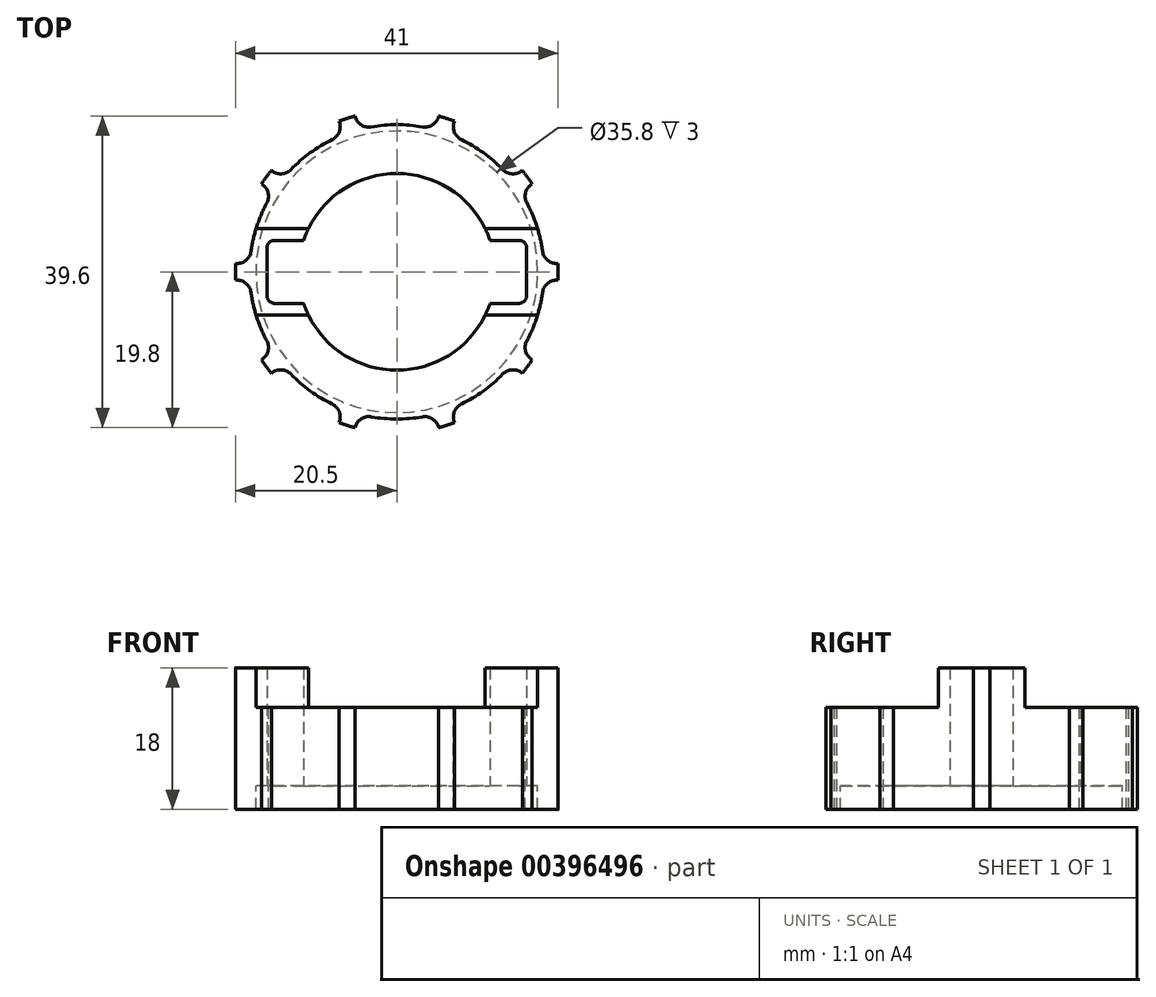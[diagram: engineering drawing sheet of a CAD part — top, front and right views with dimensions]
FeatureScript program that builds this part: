
annotation { "Feature Type Name" : "Feature", "Feature Type Description" : "" }
export const myFeature = defineFeature(function(context is Context, id is Id, definition is map)
    precondition{}
    {
        {
            var Q0;
            Q0=qCreatedBy(makeId("Top.planeOp"),FACE);
            var sketch = newSketch(context, id + "F0", { "sketchPlane" : qUnion([Q0])});
            skCircle(sketch, "E0", {"center": v(0, 0) * mm, "radius": 17.9 * mm});
            skCircle(sketch, "E1", {"center": v(0, 0) * mm, "radius": 20.5 * mm});
            skCircle(sketch, "E2", {"center": v(0, 0) * mm, "radius": 12.5 * mm});
            skLineSegment(sketch, "E3", {"start": v(0, 0) * mm, "end": v(0, 4) * mm, "construction": true});
            skLineSegment(sketch, "E4", {"start": v(0, 0) * mm, "end": v(16.5, 0) * mm, "construction": true});
            skLineSegment(sketch, "E5", {"start": v(0, 0) * mm, "end": v(-16.5, 0) * mm, "construction": true});
            skLineSegment(sketch, "E6", {"start": v(16.5, 0) * mm, "end": v(16.5, 3) * mm});
            skLineSegment(sketch, "E7", {"start": v(-16.5, 0) * mm, "end": v(-16.5, 3) * mm});
            skLineSegment(sketch, "E8", {"start": v(-15.5, 4) * mm, "end": v(-11.84, 4) * mm});
            skLineSegment(sketch, "E9", {"start": v(0, 0) * mm, "end": v(0, 20.5) * mm, "construction": true});
            skLineSegment(sketch, "E10", {"start": v(0, 0) * mm, "end": v(-3.56, 20.19) * mm, "construction": true});
            skArc(sketch, "E11", {"start": v(-5.32, 19.8) * mm, "mid": v(-4.56, 18.7) * mm, "end": v(-3.25, 18.42) * mm});
            skArc(sketch, "E12", {"start": v(-3.25, 18.42) * mm, "mid": v(-1.63, 18.63) * mm, "end": v(0, 18.7) * mm});
            skArc(sketch, "E13.MirrorCS", {"start": v(5.32, 19.8) * mm, "mid": v(4.56, 18.7) * mm, "end": v(3.25, 18.42) * mm});
            skArc(sketch, "E14.MirrorCS", {"start": v(3.25, 18.42) * mm, "mid": v(1.63, 18.63) * mm, "end": v(0, 18.7) * mm});
            skArc(sketch, "E15.1.0", {"start": v(-13.45, 13) * mm, "mid": v(-12.27, 14.11) * mm, "end": v(-11, 15.13) * mm});
            skArc(sketch, "E15.1.1", {"start": v(-15.94, 12.9) * mm, "mid": v(-14.68, 12.44) * mm, "end": v(-13.45, 13) * mm});
            skArc(sketch, "E15.1.2", {"start": v(-8.2, 16.8) * mm, "mid": v(-9.63, 16.03) * mm, "end": v(-11, 15.13) * mm});
            skArc(sketch, "E15.1.3", {"start": v(-7.34, 19.14) * mm, "mid": v(-7.3, 17.8) * mm, "end": v(-8.2, 16.8) * mm});
            skArc(sketch, "E15.2.0", {"start": v(-18.52, 2.6) * mm, "mid": v(-18.22, 4.2) * mm, "end": v(-17.78, 5.78) * mm});
            skArc(sketch, "E15.2.1", {"start": v(-20.47, 1.06) * mm, "mid": v(-19.19, 1.44) * mm, "end": v(-18.52, 2.6) * mm});
            skArc(sketch, "E15.2.2", {"start": v(-16.51, 8.78) * mm, "mid": v(-17.21, 7.3) * mm, "end": v(-17.78, 5.78) * mm});
            skArc(sketch, "E15.2.3", {"start": v(-17.19, 11.17) * mm, "mid": v(-16.37, 10.11) * mm, "end": v(-16.51, 8.78) * mm});
            skArc(sketch, "E16.2.3.0", {"start": v(-16.51, -8.78) * mm, "mid": v(-17.21, -7.3) * mm, "end": v(-17.78, -5.78) * mm});
            skArc(sketch, "E16.4.3.0", {"start": v(-17.19, -11.17) * mm, "mid": v(-16.37, -10.11) * mm, "end": v(-16.51, -8.78) * mm});
            skArc(sketch, "E16.8.3.0", {"start": v(-18.52, -2.6) * mm, "mid": v(-18.22, -4.2) * mm, "end": v(-17.78, -5.78) * mm});
            skArc(sketch, "E16.12.3.0", {"start": v(-20.47, -1.06) * mm, "mid": v(-19.19, -1.44) * mm, "end": v(-18.52, -2.6) * mm});
            skArc(sketch, "E16.2.4.0", {"start": v(-8.2, -16.8) * mm, "mid": v(-9.63, -16.03) * mm, "end": v(-11, -15.13) * mm});
            skArc(sketch, "E16.4.4.0", {"start": v(-7.34, -19.14) * mm, "mid": v(-7.3, -17.8) * mm, "end": v(-8.2, -16.8) * mm});
            skArc(sketch, "E16.8.4.0", {"start": v(-13.45, -13) * mm, "mid": v(-12.27, -14.11) * mm, "end": v(-11, -15.13) * mm});
            skArc(sketch, "E16.12.4.0", {"start": v(-15.94, -12.9) * mm, "mid": v(-14.68, -12.44) * mm, "end": v(-13.45, -13) * mm});
            skArc(sketch, "E16.2.5.0", {"start": v(3.25, -18.42) * mm, "mid": v(1.63, -18.63) * mm, "end": v(0, -18.7) * mm});
            skArc(sketch, "E16.4.5.0", {"start": v(5.32, -19.8) * mm, "mid": v(4.56, -18.7) * mm, "end": v(3.25, -18.42) * mm});
            skArc(sketch, "E16.8.5.0", {"start": v(-3.25, -18.42) * mm, "mid": v(-1.63, -18.63) * mm, "end": v(0, -18.7) * mm});
            skArc(sketch, "E16.12.5.0", {"start": v(-5.32, -19.8) * mm, "mid": v(-4.56, -18.7) * mm, "end": v(-3.25, -18.42) * mm});
            skArc(sketch, "E16.2.6.0", {"start": v(13.45, -13) * mm, "mid": v(12.27, -14.11) * mm, "end": v(11, -15.13) * mm});
            skArc(sketch, "E16.4.6.0", {"start": v(15.94, -12.9) * mm, "mid": v(14.68, -12.44) * mm, "end": v(13.45, -13) * mm});
            skArc(sketch, "E16.8.6.0", {"start": v(8.2, -16.8) * mm, "mid": v(9.63, -16.03) * mm, "end": v(11, -15.13) * mm});
            skArc(sketch, "E16.12.6.0", {"start": v(7.34, -19.14) * mm, "mid": v(7.3, -17.8) * mm, "end": v(8.2, -16.8) * mm});
            skArc(sketch, "E16.2.7.0", {"start": v(18.52, -2.6) * mm, "mid": v(18.22, -4.2) * mm, "end": v(17.78, -5.78) * mm});
            skArc(sketch, "E16.4.7.0", {"start": v(20.47, -1.06) * mm, "mid": v(19.19, -1.44) * mm, "end": v(18.52, -2.6) * mm});
            skArc(sketch, "E16.8.7.0", {"start": v(16.51, -8.78) * mm, "mid": v(17.21, -7.3) * mm, "end": v(17.78, -5.78) * mm});
            skArc(sketch, "E16.12.7.0", {"start": v(17.19, -11.17) * mm, "mid": v(16.37, -10.11) * mm, "end": v(16.51, -8.78) * mm});
            skArc(sketch, "E16.2.8.0", {"start": v(16.51, 8.78) * mm, "mid": v(17.21, 7.3) * mm, "end": v(17.78, 5.78) * mm});
            skArc(sketch, "E16.4.8.0", {"start": v(17.19, 11.17) * mm, "mid": v(16.37, 10.11) * mm, "end": v(16.51, 8.78) * mm});
            skArc(sketch, "E16.8.8.0", {"start": v(18.52, 2.6) * mm, "mid": v(18.22, 4.2) * mm, "end": v(17.78, 5.78) * mm});
            skArc(sketch, "E16.12.8.0", {"start": v(20.47, 1.06) * mm, "mid": v(19.19, 1.44) * mm, "end": v(18.52, 2.6) * mm});
            skArc(sketch, "E16.2.9.0", {"start": v(8.2, 16.8) * mm, "mid": v(9.63, 16.03) * mm, "end": v(11, 15.13) * mm});
            skArc(sketch, "E16.4.9.0", {"start": v(7.34, 19.14) * mm, "mid": v(7.3, 17.8) * mm, "end": v(8.2, 16.8) * mm});
            skArc(sketch, "E16.8.9.0", {"start": v(13.45, 13) * mm, "mid": v(12.27, 14.11) * mm, "end": v(11, 15.13) * mm});
            skArc(sketch, "E16.12.9.0", {"start": v(15.94, 12.9) * mm, "mid": v(14.68, 12.44) * mm, "end": v(13.45, 13) * mm});
            skLineSegment(sketch, "E17", {"start": v(15.5, 4) * mm, "end": v(11.84, 4) * mm});
            skLineSegment(sketch, "E18.MirrorCS", {"start": v(-16.5, 0) * mm, "end": v(-16.5, -3) * mm});
            skLineSegment(sketch, "E19.MirrorCS", {"start": v(16.5, 0) * mm, "end": v(16.5, -3) * mm});
            skLineSegment(sketch, "E20", {"start": v(15.5, -4) * mm, "end": v(11.84, -4) * mm});
            skLineSegment(sketch, "E21", {"start": v(-15.5, -4) * mm, "end": v(-11.84, -4) * mm});
            skPoint(sketch, "E22.visualSharp", {"position": v(-16.5, 4) * mm});
            skArc(sketch, "E22.filletArc", {"start": v(-15.5, 4) * mm, "mid": v(-16.2, 3.7) * mm, "end": v(-16.5, 3) * mm});
            skPoint(sketch, "E23.visualSharp", {"position": v(-16.5, -4) * mm});
            skArc(sketch, "E23.filletArc", {"start": v(-16.5, -3) * mm, "mid": v(-16.2, -3.7) * mm, "end": v(-15.5, -4) * mm});
            skPoint(sketch, "E24.visualSharp", {"position": v(16.5, -4) * mm});
            skArc(sketch, "E24.filletArc", {"start": v(15.5, -4) * mm, "mid": v(16.2, -3.7) * mm, "end": v(16.5, -3) * mm});
            skPoint(sketch, "E25.visualSharp", {"position": v(16.5, 4) * mm});
            skArc(sketch, "E25.filletArc", {"start": v(16.5, 3) * mm, "mid": v(16.2, 3.7) * mm, "end": v(15.5, 4) * mm});
            skSolve(sketch);
        }
        {
            var Q0;
            Q0=makeQuery(id+"F0.imprint","IMPRINT",FACE,{"disambiguationData":[TD([[makeQuery(id+"F0.imprint","IMPRINT",EDGE,{"derivedFrom":sQuery(id+"F0.wireOp",EDGE,"E0")}),-1.0]])]});
            extrude(context, id + "F1", {"entities" : qUnion([Q0]), "oppositeDirection" : true, "depth" : 3 * mm});
        }
        {
            var Q0;
            Q0=makeQuery(id+"F0.imprint","IMPRINT",FACE,{"disambiguationData":[TD([[makeQuery(id+"F0.imprint","IMPRINT",EDGE,{"derivedFrom":sQuery(id+"F0.wireOp",EDGE,"E0")}),-1.0]])]});
            var Q1;
            Q1=makeQuery(id+"F0.imprint","IMPRINT",FACE,{"disambiguationData":[TD([[makeQuery(id+"F0.imprint","IMPRINT",EDGE,{"derivedFrom":sQuery(id+"F0.wireOp",EDGE,"E0")}),1.0]])]});
            extrude(context, id + "F2", {"entities" : qUnion([Q0, Q1]), "operationType" : NewBodyOperationType.ADD, "depth" : 10 * mm});
        }
        {
            var Q0;
            Q0=makeQuery(id+"F2.opExtrude","CAP_FACE",FACE,{"disambiguationData":[OSD([sQuery(id+"F0.wireOp",EDGE,"E1"),sQuery(id+"F0.wireOp",EDGE,"E2"),sQuery(id+"F0.wireOp",EDGE,"E6"),sQuery(id+"F0.wireOp",EDGE,"E7"),sQuery(id+"F0.wireOp",EDGE,"E8"),sQuery(id+"F0.wireOp",EDGE,"E11"),sQuery(id+"F0.wireOp",EDGE,"E12"),sQuery(id+"F0.wireOp",EDGE,"E13.MirrorCS"),sQuery(id+"F0.wireOp",EDGE,"E14.MirrorCS"),sQuery(id+"F0.wireOp",EDGE,"E15.1.0"),sQuery(id+"F0.wireOp",EDGE,"E15.1.1"),sQuery(id+"F0.wireOp",EDGE,"E15.1.2"),sQuery(id+"F0.wireOp",EDGE,"E15.1.3"),sQuery(id+"F0.wireOp",EDGE,"E15.2.0"),sQuery(id+"F0.wireOp",EDGE,"E15.2.1"),sQuery(id+"F0.wireOp",EDGE,"E15.2.2"),sQuery(id+"F0.wireOp",EDGE,"E15.2.3"),sQuery(id+"F0.wireOp",EDGE,"E16.2.3.0"),sQuery(id+"F0.wireOp",EDGE,"E16.4.3.0"),sQuery(id+"F0.wireOp",EDGE,"E16.8.3.0"),sQuery(id+"F0.wireOp",EDGE,"E16.12.3.0"),sQuery(id+"F0.wireOp",EDGE,"E16.2.4.0"),sQuery(id+"F0.wireOp",EDGE,"E16.4.4.0"),sQuery(id+"F0.wireOp",EDGE,"E16.8.4.0"),sQuery(id+"F0.wireOp",EDGE,"E16.12.4.0"),sQuery(id+"F0.wireOp",EDGE,"E16.2.5.0"),sQuery(id+"F0.wireOp",EDGE,"E16.4.5.0"),sQuery(id+"F0.wireOp",EDGE,"E16.8.5.0"),sQuery(id+"F0.wireOp",EDGE,"E16.12.5.0"),sQuery(id+"F0.wireOp",EDGE,"E16.2.6.0"),sQuery(id+"F0.wireOp",EDGE,"E16.4.6.0"),sQuery(id+"F0.wireOp",EDGE,"E16.8.6.0"),sQuery(id+"F0.wireOp",EDGE,"E16.12.6.0"),sQuery(id+"F0.wireOp",EDGE,"E16.2.7.0"),sQuery(id+"F0.wireOp",EDGE,"E16.4.7.0"),sQuery(id+"F0.wireOp",EDGE,"E16.8.7.0"),sQuery(id+"F0.wireOp",EDGE,"E16.12.7.0"),sQuery(id+"F0.wireOp",EDGE,"E16.2.8.0"),sQuery(id+"F0.wireOp",EDGE,"E16.4.8.0"),sQuery(id+"F0.wireOp",EDGE,"E16.8.8.0"),sQuery(id+"F0.wireOp",EDGE,"E16.12.8.0"),sQuery(id+"F0.wireOp",EDGE,"E16.2.9.0"),sQuery(id+"F0.wireOp",EDGE,"E16.4.9.0"),sQuery(id+"F0.wireOp",EDGE,"E16.8.9.0"),sQuery(id+"F0.wireOp",EDGE,"E16.12.9.0"),sQuery(id+"F0.wireOp",EDGE,"E17"),sQuery(id+"F0.wireOp",EDGE,"E18.MirrorCS"),sQuery(id+"F0.wireOp",EDGE,"E19.MirrorCS"),sQuery(id+"F0.wireOp",EDGE,"E20"),sQuery(id+"F0.wireOp",EDGE,"E21"),sQuery(id+"F0.wireOp",EDGE,"E22.filletArc"),sQuery(id+"F0.wireOp",EDGE,"E23.filletArc"),sQuery(id+"F0.wireOp",EDGE,"E24.filletArc"),sQuery(id+"F0.wireOp",EDGE,"E25.filletArc")])],"isStart":false});
            var sketch = newSketch(context, id + "F3", { "sketchPlane" : qUnion([Q0])});
            skArc(sketch, "E26.0", {"start": v(-11.84, -4) * mm, "mid": v(0, -12.5) * mm, "end": v(11.84, -4) * mm});
            skArc(sketch, "E27.0.0", {"start": v(8.2, 16.8) * mm, "mid": v(7.3, 17.8) * mm, "end": v(7.34, 19.14) * mm});
            skArc(sketch, "E27.0.1", {"start": v(7.34, 19.14) * mm, "mid": v(6.33, 19.5) * mm, "end": v(5.32, 19.8) * mm});
            skArc(sketch, "E27.0.2", {"start": v(5.32, 19.8) * mm, "mid": v(4.56, 18.7) * mm, "end": v(3.25, 18.42) * mm});
            skArc(sketch, "E27.0.3", {"start": v(3.25, 18.42) * mm, "mid": v(0, 18.7) * mm, "end": v(-3.25, 18.42) * mm});
            skArc(sketch, "E27.0.4", {"start": v(-3.25, 18.42) * mm, "mid": v(-4.56, 18.7) * mm, "end": v(-5.32, 19.8) * mm});
            skArc(sketch, "E27.0.5", {"start": v(-5.32, 19.8) * mm, "mid": v(-6.33, 19.5) * mm, "end": v(-7.34, 19.14) * mm});
            skArc(sketch, "E27.0.6", {"start": v(-7.34, 19.14) * mm, "mid": v(-7.3, 17.8) * mm, "end": v(-8.2, 16.8) * mm});
            skArc(sketch, "E27.0.7", {"start": v(-8.2, 16.8) * mm, "mid": v(-11, 15.13) * mm, "end": v(-13.45, 13) * mm});
            skArc(sketch, "E27.0.8", {"start": v(-13.45, 13) * mm, "mid": v(-14.68, 12.44) * mm, "end": v(-15.94, 12.9) * mm});
            skArc(sketch, "E27.0.9", {"start": v(-15.94, 12.9) * mm, "mid": v(-16.58, 12.05) * mm, "end": v(-17.19, 11.17) * mm});
            skArc(sketch, "E27.0.10", {"start": v(-17.19, 11.17) * mm, "mid": v(-16.37, 10.11) * mm, "end": v(-16.51, 8.78) * mm});
            skArc(sketch, "E27.0.11", {"start": v(-16.51, 8.78) * mm, "mid": v(-17.78, 5.78) * mm, "end": v(-18.52, 2.6) * mm});
            skArc(sketch, "E27.0.12", {"start": v(-18.52, 2.6) * mm, "mid": v(-19.19, 1.44) * mm, "end": v(-20.47, 1.06) * mm});
            skArc(sketch, "E27.0.13", {"start": v(-20.47, 1.06) * mm, "mid": v(-20.5, 0) * mm, "end": v(-20.47, -1.06) * mm});
            skArc(sketch, "E27.0.14", {"start": v(-20.47, -1.06) * mm, "mid": v(-19.19, -1.44) * mm, "end": v(-18.52, -2.6) * mm});
            skArc(sketch, "E27.0.15", {"start": v(-18.52, -2.6) * mm, "mid": v(-17.78, -5.78) * mm, "end": v(-16.51, -8.78) * mm});
            skArc(sketch, "E27.0.16", {"start": v(-16.51, -8.78) * mm, "mid": v(-16.37, -10.11) * mm, "end": v(-17.19, -11.17) * mm});
            skArc(sketch, "E27.0.17", {"start": v(-17.19, -11.17) * mm, "mid": v(-16.58, -12.05) * mm, "end": v(-15.94, -12.9) * mm});
            skArc(sketch, "E27.0.18", {"start": v(-15.94, -12.9) * mm, "mid": v(-14.68, -12.44) * mm, "end": v(-13.45, -13) * mm});
            skArc(sketch, "E27.0.19", {"start": v(-13.45, -13) * mm, "mid": v(-11, -15.13) * mm, "end": v(-8.2, -16.8) * mm});
            skArc(sketch, "E27.0.20", {"start": v(-8.2, -16.8) * mm, "mid": v(-7.3, -17.8) * mm, "end": v(-7.34, -19.14) * mm});
            skArc(sketch, "E27.0.21", {"start": v(-7.34, -19.14) * mm, "mid": v(-6.33, -19.5) * mm, "end": v(-5.32, -19.8) * mm});
            skArc(sketch, "E27.0.22", {"start": v(-5.32, -19.8) * mm, "mid": v(-4.56, -18.7) * mm, "end": v(-3.25, -18.42) * mm});
            skArc(sketch, "E27.0.23", {"start": v(-3.25, -18.42) * mm, "mid": v(0, -18.7) * mm, "end": v(3.25, -18.42) * mm});
            skArc(sketch, "E27.0.24", {"start": v(3.25, -18.42) * mm, "mid": v(4.56, -18.7) * mm, "end": v(5.32, -19.8) * mm});
            skArc(sketch, "E27.0.25", {"start": v(5.32, -19.8) * mm, "mid": v(6.33, -19.5) * mm, "end": v(7.34, -19.14) * mm});
            skArc(sketch, "E27.0.26", {"start": v(7.34, -19.14) * mm, "mid": v(7.3, -17.8) * mm, "end": v(8.2, -16.8) * mm});
            skArc(sketch, "E27.0.27", {"start": v(8.2, -16.8) * mm, "mid": v(11, -15.13) * mm, "end": v(13.45, -13) * mm});
            skArc(sketch, "E27.0.28", {"start": v(13.45, -13) * mm, "mid": v(14.68, -12.44) * mm, "end": v(15.94, -12.9) * mm});
            skArc(sketch, "E27.0.29", {"start": v(15.94, -12.9) * mm, "mid": v(16.58, -12.05) * mm, "end": v(17.19, -11.17) * mm});
            skArc(sketch, "E27.0.30", {"start": v(17.19, -11.17) * mm, "mid": v(16.37, -10.11) * mm, "end": v(16.51, -8.78) * mm});
            skArc(sketch, "E27.0.31", {"start": v(16.51, -8.78) * mm, "mid": v(17.78, -5.78) * mm, "end": v(18.52, -2.6) * mm});
            skArc(sketch, "E27.0.32", {"start": v(18.52, -2.6) * mm, "mid": v(19.19, -1.44) * mm, "end": v(20.47, -1.06) * mm});
            skArc(sketch, "E27.0.33", {"start": v(20.47, -1.06) * mm, "mid": v(20.5, 0) * mm, "end": v(20.47, 1.06) * mm});
            skArc(sketch, "E27.0.34", {"start": v(20.47, 1.06) * mm, "mid": v(19.19, 1.44) * mm, "end": v(18.52, 2.6) * mm});
            skArc(sketch, "E27.0.35", {"start": v(18.52, 2.6) * mm, "mid": v(17.78, 5.78) * mm, "end": v(16.51, 8.78) * mm});
            skArc(sketch, "E27.0.36", {"start": v(16.51, 8.78) * mm, "mid": v(16.37, 10.11) * mm, "end": v(17.19, 11.17) * mm});
            skArc(sketch, "E27.0.37", {"start": v(17.19, 11.17) * mm, "mid": v(16.58, 12.05) * mm, "end": v(15.94, 12.9) * mm});
            skArc(sketch, "E27.0.38", {"start": v(15.94, 12.9) * mm, "mid": v(14.68, 12.44) * mm, "end": v(13.45, 13) * mm});
            skArc(sketch, "E27.0.39", {"start": v(13.45, 13) * mm, "mid": v(11, 15.13) * mm, "end": v(8.2, 16.8) * mm});
            skLineSegment(sketch, "E28.0", {"start": v(17.87, -5.5) * mm, "end": v(11.22, -5.5) * mm});
            skLineSegment(sketch, "E29.MirrorCS", {"start": v(17.87, 5.5) * mm, "end": v(11.22, 5.5) * mm});
            skLineSegment(sketch, "E30.MirrorCS", {"start": v(-17.87, -5.5) * mm, "end": v(-11.22, -5.5) * mm});
            skLineSegment(sketch, "E31.MirrorCS", {"start": v(-17.87, 5.5) * mm, "end": v(-11.22, 5.5) * mm});
            skSolve(sketch);
        }
        {
            var Q0;
            {var subQ8=sQuery(id+"F3.wireOp",EDGE,"E27.0.32");Q0=makeQuery(id+"F3.imprint","IMPRINT",FACE,{"disambiguationData":[TD([[makeQuery(id+"F3.imprint","IMPRINT",EDGE,{"derivedFrom":subQ8}),-1.0]])]});}
            var Q1;
            {var subQ7=sQuery(id+"F3.wireOp",EDGE,"E27.0.12");Q1=makeQuery(id+"F3.imprint","IMPRINT",FACE,{"disambiguationData":[TD([[makeQuery(id+"F3.imprint","IMPRINT",EDGE,{"derivedFrom":subQ7}),-1.0]])]});}
            extrude(context, id + "F4", {"entities" : qUnion([Q0, Q1]), "operationType" : NewBodyOperationType.ADD, "depth" : 5 * mm});
        }
    });
